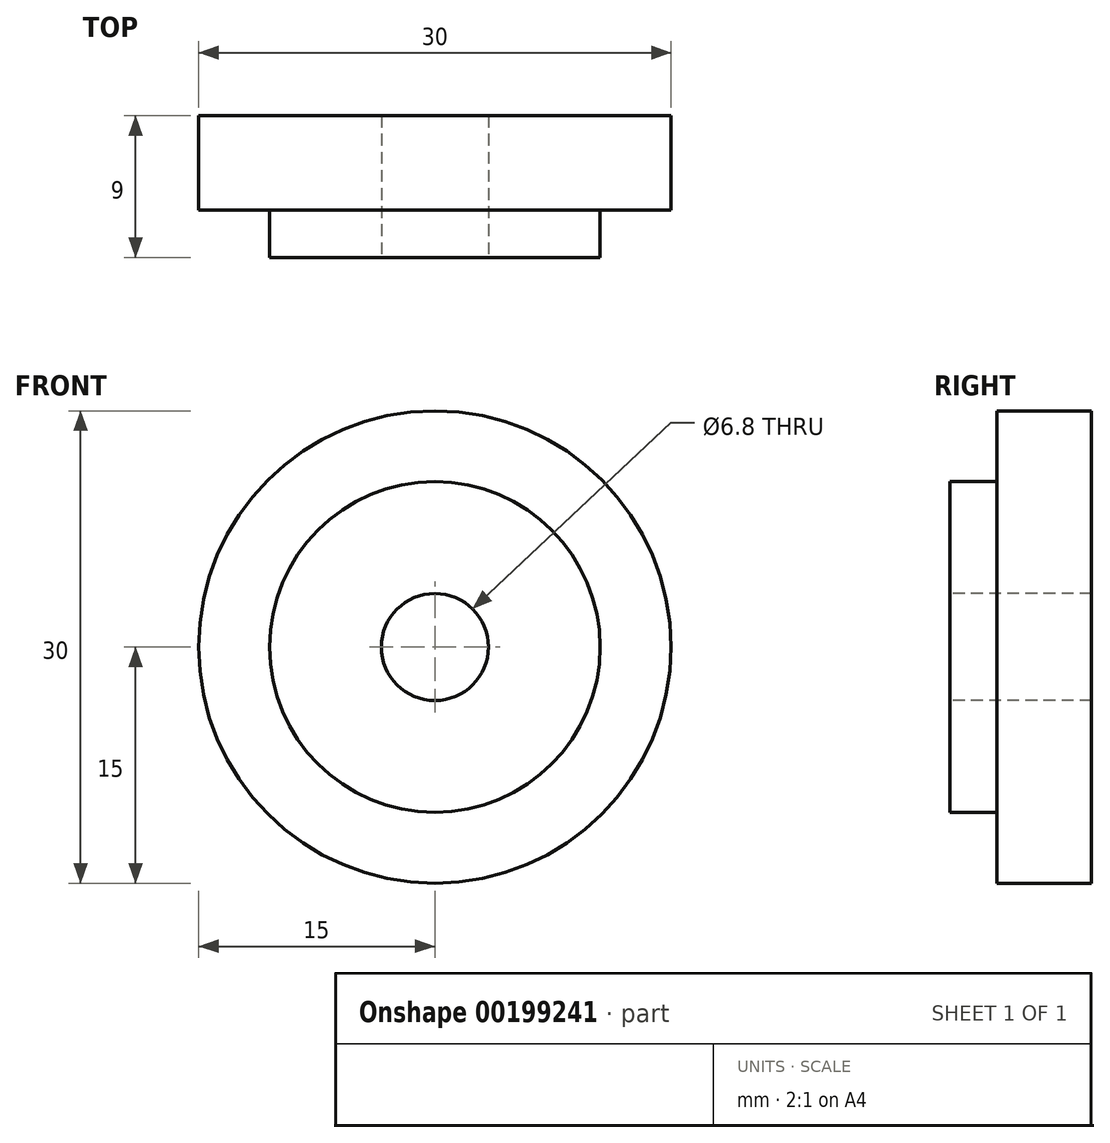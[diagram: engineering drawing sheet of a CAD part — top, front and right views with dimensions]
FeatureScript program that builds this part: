
annotation { "Feature Type Name" : "Feature", "Feature Type Description" : "" }
export const myFeature = defineFeature(function(context is Context, id is Id, definition is map)
    precondition{}
    {
        {
            var Q0;
            Q0=qCreatedBy(makeId("Front.planeOp"),FACE);
            var sketch = newSketch(context, id + "F0", { "sketchPlane" : qUnion([Q0])});
            skCircle(sketch, "E0", {"center": v(0, 0) * mm, "radius": 15 * mm});
            skSolve(sketch);
        }
        {
            var Q0;
            Q0 = qSketchRegion(id + "F0", true);
            extrude(context, id + "F1", {"entities" : qUnion([Q0]), "depth" : 6 * mm});
        }
        {
            var Q0;
            Q0=makeQuery(id+"F1.opExtrude","CAP_FACE",FACE,{"disambiguationData":[OSD([sQuery(id+"F0.wireOp",EDGE,"E0")])],"isStart":false});
            var sketch = newSketch(context, id + "F2", { "sketchPlane" : qUnion([Q0])});
            skCircle(sketch, "E1", {"center": v(0, 0) * mm, "radius": 10.5 * mm});
            skSolve(sketch);
        }
        {
            var Q0;
            Q0 = qSketchRegion(id + "F2", true);
            extrude(context, id + "F3", {"entities" : qUnion([Q0]), "operationType" : NewBodyOperationType.ADD, "depth" : 3 * mm});
        }
        {
            var Q0;
            Q0=makeQuery(id+"F3.opExtrude","CAP_FACE",FACE,{"disambiguationData":[OSD([sQuery(id+"F2.wireOp",EDGE,"E1")])],"isStart":false});
            var sketch = newSketch(context, id + "F4", { "sketchPlane" : qUnion([Q0])});
            skPoint(sketch, "E2", {"position": v(0, 0) * mm});
            skSolve(sketch);
        }
        {
            var Q0;
            Q0=sQuery(id+"F4.wireOp",VERTEX,"E2");
            var Q1;
            Q1=makeQuery(id+"F1.opExtrude","SWEPT_BODY",BODY,{"disambiguationData":[OSD([sQuery(id+"F0.wireOp",EDGE,"E0")])]});
            hole(context, id + "F5", {"style" : HoleStyle.SIMPLE, "endStyle" : HoleEndStyle.BLIND, "holeDiameter" : 6.8 * mm, "holeDepth" : 10 * mm, "startFromSketch" : true, "locations" : qUnion([Q0]), "scope" : qUnion([Q1])});
        }
    });
